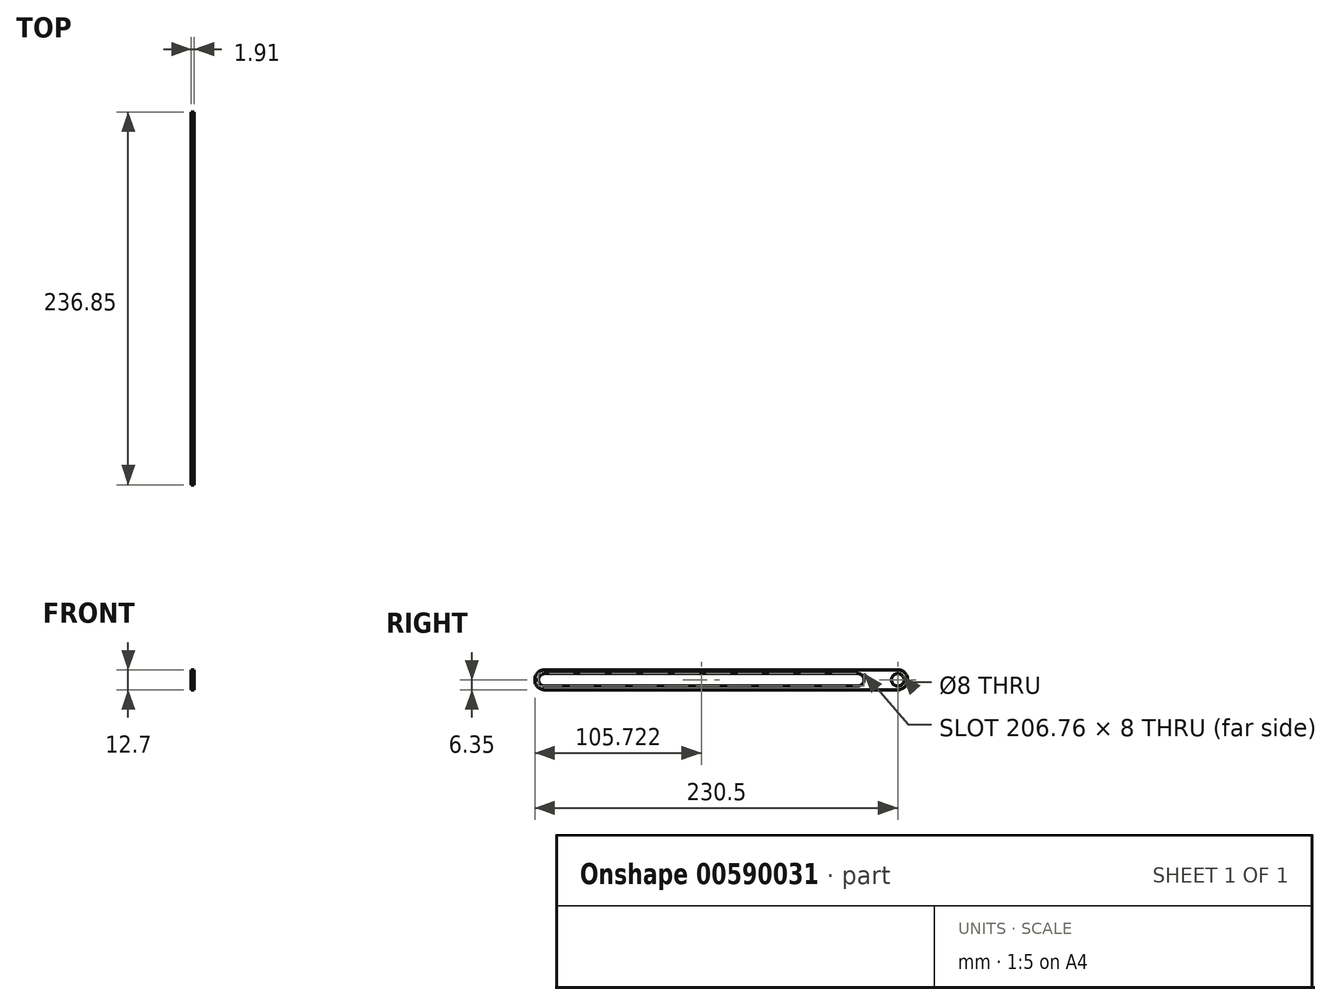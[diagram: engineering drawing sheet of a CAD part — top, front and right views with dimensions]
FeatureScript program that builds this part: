
annotation { "Feature Type Name" : "Feature", "Feature Type Description" : "" }
export const myFeature = defineFeature(function(context is Context, id is Id, definition is map)
    precondition{}
    {
        {
            var Q0;
            Q0=qCreatedBy(makeId("Right.planeOp"),FACE);
            var sketch = newSketch(context, id + "F0", { "sketchPlane" : qUnion([Q0])});
            skArc(sketch, "E0", {"start": v(0, -6.35) * mm, "mid": v(6.35, 0) * mm, "end": v(0, 6.35) * mm});
            skArc(sketch, "E1", {"start": v(-224.16, 6.35) * mm, "mid": v(-230.5, 0) * mm, "end": v(-224.16, -6.35) * mm});
            skLineSegment(sketch, "E2", {"start": v(-224.16, 6.35) * mm, "end": v(0, 6.35) * mm});
            skLineSegment(sketch, "E3", {"start": v(-224.16, -6.35) * mm, "end": v(0, -6.35) * mm});
            skCircle(sketch, "E4", {"center": v(0, 0) * mm, "radius": 4 * mm});
            skArc(sketch, "E5", {"start": v(-224.16, 4) * mm, "mid": v(-228.16, 0) * mm, "end": v(-224.16, -4) * mm});
            skArc(sketch, "E6", {"start": v(-25.4, -4) * mm, "mid": v(-21.4, 0) * mm, "end": v(-25.4, 4) * mm});
            skLineSegment(sketch, "E7", {"start": v(-224.16, 4) * mm, "end": v(-25.4, 4) * mm});
            skLineSegment(sketch, "E8", {"start": v(-224.16, -4) * mm, "end": v(-25.4, -4) * mm});
            skSolve(sketch);
        }
        {
            var Q0;
            Q0 = qSketchRegion(id + "F0", true);
            extrude(context, id + "F1", {"entities" : qUnion([Q0]), "depth" : 1.9 * mm, "offsetDistance" : 25.4 * mm});
        }
    });
